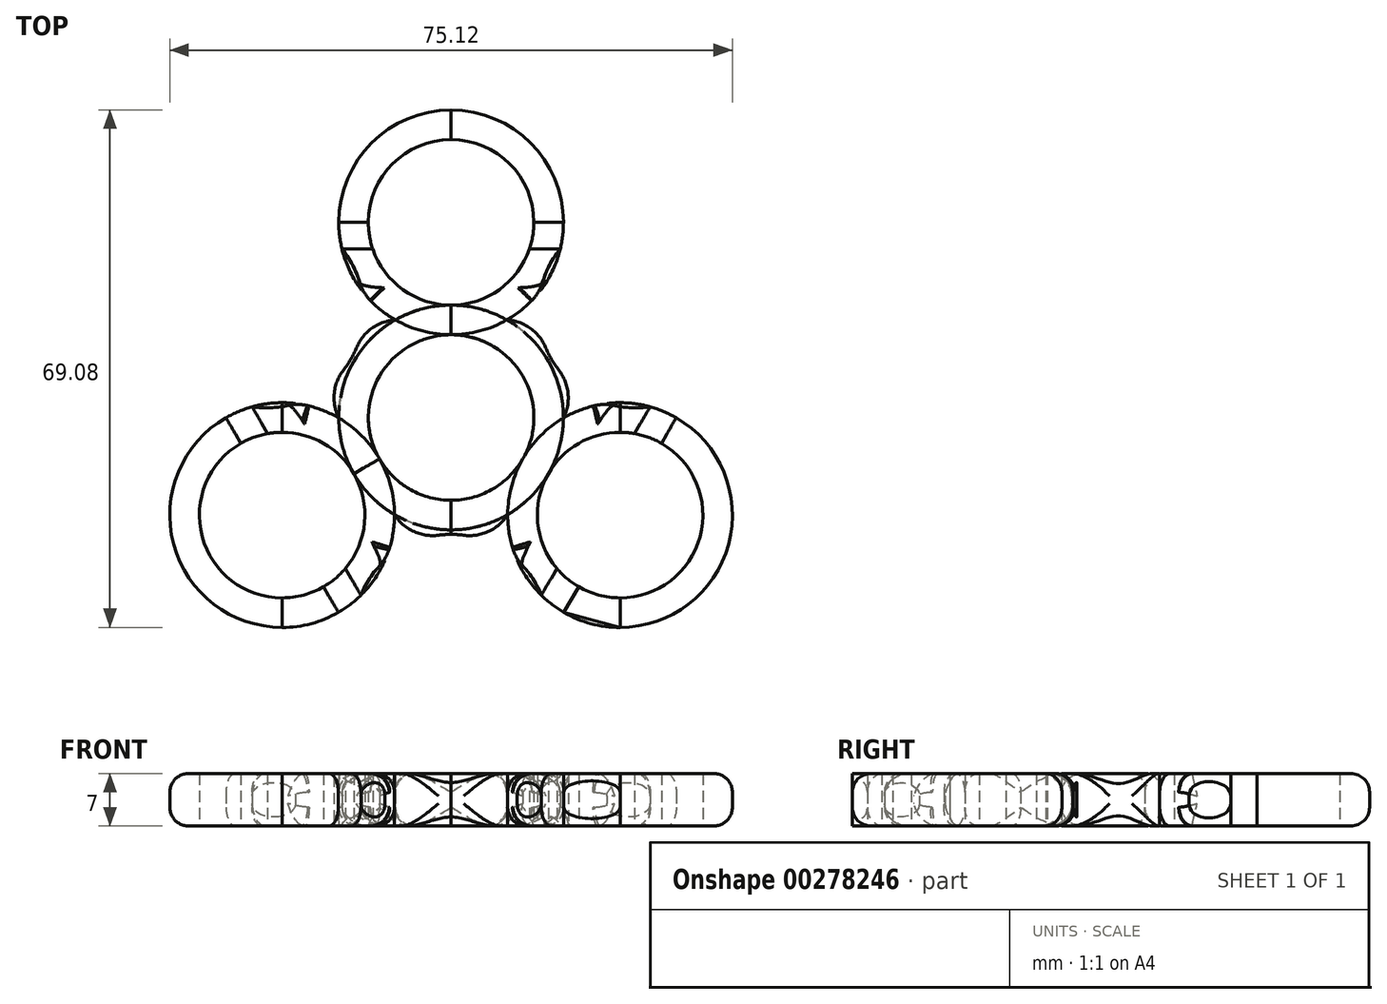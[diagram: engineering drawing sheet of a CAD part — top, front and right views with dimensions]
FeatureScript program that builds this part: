
annotation { "Feature Type Name" : "Feature", "Feature Type Description" : "" }
export const myFeature = defineFeature(function(context is Context, id is Id, definition is map)
    precondition{}
    {
        {
            var Q0;
            Q0=qCreatedBy(makeId("Top.planeOp"),FACE);
            var sketch = newSketch(context, id + "F0", { "sketchPlane" : qUnion([Q0])});
            skCircle(sketch, "E0", {"center": v(3.55, 32.56) * mm, "radius": 11.05 * mm});
            skCircle(sketch, "E1", {"center": v(3.55, 32.56) * mm, "radius": 15 * mm});
            skLineSegment(sketch, "E2", {"start": v(3.55, 32.56) * mm, "end": v(3.55, -19.54) * mm});
            skLineSegment(sketch, "E3", {"start": v(3.55, 17.56) * mm, "end": v(3.55, 6.5) * mm});
            skCircle(sketch, "E4", {"center": v(3.55, 6.5) * mm, "radius": 15 * mm});
            skCircle(sketch, "E5", {"center": v(3.55, 6.5) * mm, "radius": 11.05 * mm});
            skCircle(sketch, "E6.1.0", {"center": v(-19.01, -6.52) * mm, "radius": 11.05 * mm});
            skCircle(sketch, "E6.1.1", {"center": v(-19.01, -6.52) * mm, "radius": 15 * mm});
            skCircle(sketch, "E6.2.0", {"center": v(26.1, -6.52) * mm, "radius": 11.05 * mm});
            skCircle(sketch, "E6.2.1", {"center": v(26.1, -6.52) * mm, "radius": 15 * mm});
            skLineSegment(sketch, "E7", {"start": v(-19.01, -6.52) * mm, "end": v(-19.01, 16.07) * mm});
            skLineSegment(sketch, "E8", {"start": v(3.55, 32.56) * mm, "end": v(-11.45, 32.56) * mm});
            skLineSegment(sketch, "E9", {"start": v(-11.45, 32.56) * mm, "end": v(3.55, 32.56) * mm});
            skLineSegment(sketch, "E10", {"start": v(3.55, 32.56) * mm, "end": v(18.55, 32.56) * mm});
            skLineSegment(sketch, "E11", {"start": v(-19.01, -6.52) * mm, "end": v(-19.01, -21.52) * mm});
            skLineSegment(sketch, "E12", {"start": v(26.1, -6.52) * mm, "end": v(26.1, -21.52) * mm});
            skLineSegment(sketch, "E13", {"start": v(26.1, -21.52) * mm, "end": v(26.1, -6.52) * mm});
            skLineSegment(sketch, "E14", {"start": v(26.1, 8.48) * mm, "end": v(26.1, -6.52) * mm});
            skLineSegment(sketch, "E15", {"start": v(-19.01, -6.52) * mm, "end": v(-6.02, 0.98) * mm});
            skLineSegment(sketch, "E16", {"start": v(26.1, -6.52) * mm, "end": v(13.12, 0.98) * mm});
            skLineSegment(sketch, "E17", {"start": v(13.12, 0.98) * mm, "end": v(26.1, -6.52) * mm});
            skLineSegment(sketch, "E18", {"start": v(26.1, -6.52) * mm, "end": v(18.6, -19.5) * mm});
            skLineSegment(sketch, "E19", {"start": v(-19.01, -6.52) * mm, "end": v(-11.51, -19.5) * mm});
            skLineSegment(sketch, "E20", {"start": v(-11.51, -19.5) * mm, "end": v(-19.01, -6.52) * mm});
            skLineSegment(sketch, "E21", {"start": v(-19.01, -6.52) * mm, "end": v(-26.51, 6.47) * mm});
            skLineSegment(sketch, "E22", {"start": v(26.1, -6.52) * mm, "end": v(33.6, 6.47) * mm});
            skLineSegment(sketch, "E23", {"start": v(3.55, 32.56) * mm, "end": v(-5.63, 20.7) * mm, "construction": true});
            skLineSegment(sketch, "E24", {"start": v(-5.63, 20.7) * mm, "end": v(-1.04, 26.63) * mm, "construction": true});
            skLineSegment(sketch, "E25", {"start": v(26.1, -21.52) * mm, "end": v(18.6, -19.5) * mm});
            skLineSegment(sketch, "E26", {"start": v(26.1, -6.52) * mm, "end": v(19.61, -2.77) * mm});
            skLineSegment(sketch, "E27", {"start": v(16.54, -1) * mm, "end": v(22.86, -4.64) * mm});
            skLineSegment(sketch, "E28", {"start": v(22.86, -4.64) * mm, "end": v(15.6, -17.22) * mm});
            skLineSegment(sketch, "E29", {"start": v(-9.44, -1) * mm, "end": v(-15.76, -4.64) * mm});
            skLineSegment(sketch, "E30", {"start": v(-15.76, -4.64) * mm, "end": v(-8.5, -17.22) * mm});
            skLineSegment(sketch, "E31", {"start": v(-15.76, -4.64) * mm, "end": v(-23.03, 7.94) * mm});
            skLineSegment(sketch, "E32", {"start": v(22.86, -4.64) * mm, "end": v(30.12, 7.94) * mm});
            skLineSegment(sketch, "E33", {"start": v(3.55, 21.5) * mm, "end": v(3.55, 29) * mm});
            skLineSegment(sketch, "E34", {"start": v(3.55, 29) * mm, "end": v(-11.03, 29) * mm});
            skLineSegment(sketch, "E35", {"start": v(3.55, 29) * mm, "end": v(18.12, 29) * mm});
            skArc(sketch, "E36", {"start": v(15.6, -17.22) * mm, "mid": v(3.55, -9.1) * mm, "end": v(-8.5, -17.22) * mm});
            skArc(sketch, "E37", {"start": v(-23.03, 7.94) * mm, "mid": v(-9.8, 14.36) * mm, "end": v(-11.03, 29) * mm});
            skArc(sketch, "E38", {"start": v(18.12, 29) * mm, "mid": v(16.9, 14.36) * mm, "end": v(30.12, 7.94) * mm});
            skLineSegment(sketch, "E39", {"start": v(3.55, 6.5) * mm, "end": v(3.55, 47.56) * mm});
            skSolve(sketch);
        }
        {
            var Q0;
            {var subQ0=sQuery(id+"F0.wireOp",EDGE,"E4");var subQ1=sQuery(id+"F0.wireOp",EDGE,"E1");var subQ2=makeQuery(id+"F0.imprint","INTERSECT",VERTEX,{"disambiguationData":[OD(1.0)],"derivedFrom":[subQ1,subQ0]});Q0=makeQuery(id+"F0.imprint","IMPRINT",FACE,{"disambiguationData":[TD([[makeQuery(id+"F0.imprint","IMPRINT",EDGE,{"disambiguationData":[TD([[subQ2,1.0]])],"derivedFrom":subQ0}),1.0]])]});}
            var Q1;
            {var subQ0=sQuery(id+"F0.wireOp",EDGE,"E13");var subQ1=sQuery(id+"F0.wireOp",EDGE,"E6.2.0");var subQ2=makeQuery(id+"F0.imprint","INTERSECT",VERTEX,{"derivedFrom":[subQ1,subQ0]});Q1=makeQuery(id+"F0.imprint","IMPRINT",FACE,{"disambiguationData":[TD([[makeQuery(id+"F0.imprint","IMPRINT",EDGE,{"disambiguationData":[TD([[subQ2,-1.0]])],"derivedFrom":subQ1}),-1.0]])]});}
            var Q2;
            {var subQ1=sQuery(id+"F0.wireOp",EDGE,"E4");var subQ3=sQuery(id+"F0.wireOp",EDGE,"E6.1.1");var subQ4=makeQuery(id+"F0.imprint","INTERSECT",VERTEX,{"disambiguationData":[OD(0.0)],"derivedFrom":[subQ1,subQ3]});Q2=makeQuery(id+"F0.imprint","IMPRINT",FACE,{"disambiguationData":[TD([[makeQuery(id+"F0.imprint","IMPRINT",EDGE,{"disambiguationData":[TD([[subQ4,1.0]])],"derivedFrom":subQ3}),1.0]])]});}
            var Q3;
            {var subQ0=sQuery(id+"F0.wireOp",EDGE,"E5");var subQ1=sQuery(id+"F0.wireOp",EDGE,"E2");var subQ2=makeQuery(id+"F0.imprint","INTERSECT",VERTEX,{"derivedFrom":[subQ1,subQ0]});Q3=makeQuery(id+"F0.imprint","IMPRINT",FACE,{"disambiguationData":[TD([[makeQuery(id+"F0.imprint","IMPRINT",EDGE,{"disambiguationData":[TD([[subQ2,-1.0]])],"derivedFrom":subQ1}),1.0]])]});}
            var Q4;
            {var subQ0=sQuery(id+"F0.wireOp",EDGE,"E22");var subQ1=sQuery(id+"F0.wireOp",EDGE,"E6.2.0");var subQ2=makeQuery(id+"F0.imprint","INTERSECT",VERTEX,{"derivedFrom":[subQ1,subQ0]});Q4=makeQuery(id+"F0.imprint","IMPRINT",FACE,{"disambiguationData":[TD([[makeQuery(id+"F0.imprint","IMPRINT",EDGE,{"disambiguationData":[TD([[subQ2,-1.0]])],"derivedFrom":subQ1}),-1.0]])]});}
            var Q5;
            {var subQ0=sQuery(id+"F0.wireOp",EDGE,"E38");var subQ1=sQuery(id+"F0.wireOp",EDGE,"E6.2.1");var subQ2=makeQuery(id+"F0.imprint","INTERSECT",VERTEX,{"derivedFrom":[subQ1,subQ0]});Q5=makeQuery(id+"F0.imprint","IMPRINT",FACE,{"disambiguationData":[TD([[makeQuery(id+"F0.imprint","IMPRINT",EDGE,{"disambiguationData":[TD([[subQ2,-1.0]])],"derivedFrom":subQ1}),1.0]])]});}
            var Q6;
            {var subQ0=sQuery(id+"F0.wireOp",EDGE,"E17");Q6=makeQuery(id+"F0.imprint","IMPRINT",FACE,{"disambiguationData":[TD([[makeQuery(id+"F0.imprint","IMPRINT",EDGE,{"derivedFrom":subQ0}),-1.0]])]});}
            var Q7;
            {var subQ0=sQuery(id+"F0.wireOp",EDGE,"E18");var subQ1=sQuery(id+"F0.wireOp",EDGE,"E6.2.0");var subQ2=makeQuery(id+"F0.imprint","INTERSECT",VERTEX,{"derivedFrom":[subQ1,subQ0]});Q7=makeQuery(id+"F0.imprint","IMPRINT",FACE,{"disambiguationData":[TD([[makeQuery(id+"F0.imprint","IMPRINT",EDGE,{"disambiguationData":[TD([[subQ2,1.0]])],"derivedFrom":subQ1}),-1.0]])]});}
            var Q8;
            {var subQ0=sQuery(id+"F0.wireOp",EDGE,"E32");var subQ1=sQuery(id+"F0.wireOp",EDGE,"E6.2.0");var subQ2=makeQuery(id+"F0.imprint","INTERSECT",VERTEX,{"derivedFrom":[subQ1,subQ0]});Q8=makeQuery(id+"F0.imprint","IMPRINT",FACE,{"disambiguationData":[TD([[makeQuery(id+"F0.imprint","IMPRINT",EDGE,{"disambiguationData":[TD([[subQ2,-1.0]])],"derivedFrom":subQ1}),-1.0]])]});}
            var Q9;
            {var subQ0=sQuery(id+"F0.wireOp",EDGE,"E4");var subQ1=sQuery(id+"F0.wireOp",EDGE,"E1");var subQ2=makeQuery(id+"F0.imprint","INTERSECT",VERTEX,{"disambiguationData":[OD(0.0)],"derivedFrom":[subQ1,subQ0]});Q9=makeQuery(id+"F0.imprint","IMPRINT",FACE,{"disambiguationData":[TD([[makeQuery(id+"F0.imprint","IMPRINT",EDGE,{"disambiguationData":[TD([[subQ2,-1.0]])],"derivedFrom":subQ0}),1.0]])]});}
            var Q10;
            {var subQ0=sQuery(id+"F0.wireOp",EDGE,"E36");var subQ2=sQuery(id+"F0.wireOp",EDGE,"E6.1.1");var subQ6=makeQuery(id+"F0.imprint","INTERSECT",VERTEX,{"derivedFrom":[subQ2,subQ0]});Q10=makeQuery(id+"F0.imprint","IMPRINT",FACE,{"disambiguationData":[TD([[makeQuery(id+"F0.imprint","IMPRINT",EDGE,{"disambiguationData":[TD([[subQ6,-1.0]])],"derivedFrom":subQ2}),1.0]])]});}
            var Q11;
            {var subQ0=sQuery(id+"F0.wireOp",EDGE,"E36");var subQ1=sQuery(id+"F0.wireOp",EDGE,"E2");var subQ2=makeQuery(id+"F0.imprint","INTERSECT",VERTEX,{"derivedFrom":[subQ1,subQ0]});Q11=makeQuery(id+"F0.imprint","IMPRINT",FACE,{"disambiguationData":[TD([[makeQuery(id+"F0.imprint","IMPRINT",EDGE,{"disambiguationData":[TD([[subQ2,1.0]])],"derivedFrom":subQ1}),-1.0]])]});}
            var Q12;
            {var subQ0=sQuery(id+"F0.wireOp",EDGE,"E36");var subQ1=sQuery(id+"F0.wireOp",EDGE,"E2");var subQ2=makeQuery(id+"F0.imprint","INTERSECT",VERTEX,{"derivedFrom":[subQ1,subQ0]});Q12=makeQuery(id+"F0.imprint","IMPRINT",FACE,{"disambiguationData":[TD([[makeQuery(id+"F0.imprint","IMPRINT",EDGE,{"disambiguationData":[TD([[subQ2,1.0]])],"derivedFrom":subQ1}),1.0]])]});}
            var Q13;
            {var subQ1=sQuery(id+"F0.wireOp",EDGE,"E4");var subQ3=sQuery(id+"F0.wireOp",EDGE,"E6.1.1");var subQ4=makeQuery(id+"F0.imprint","INTERSECT",VERTEX,{"disambiguationData":[OD(1.0)],"derivedFrom":[subQ1,subQ3]});Q13=makeQuery(id+"F0.imprint","IMPRINT",FACE,{"disambiguationData":[TD([[makeQuery(id+"F0.imprint","IMPRINT",EDGE,{"disambiguationData":[TD([[subQ4,-1.0]])],"derivedFrom":subQ3}),1.0]])]});}
            var Q14;
            {var subQ0=sQuery(id+"F0.wireOp",EDGE,"E39");var subQ1=sQuery(id+"F0.wireOp",EDGE,"E0");var subQ2=makeQuery(id+"F0.imprint","INTERSECT",VERTEX,{"derivedFrom":[subQ1,subQ0]});Q14=makeQuery(id+"F0.imprint","IMPRINT",FACE,{"disambiguationData":[TD([[makeQuery(id+"F0.imprint","IMPRINT",EDGE,{"disambiguationData":[TD([[subQ2,-1.0]])],"derivedFrom":subQ1}),-1.0]])]});}
            var Q15;
            {var subQ0=sQuery(id+"F0.wireOp",EDGE,"E37");var subQ1=sQuery(id+"F0.wireOp",EDGE,"E1");var subQ2=makeQuery(id+"F0.imprint","INTERSECT",VERTEX,{"derivedFrom":[subQ1,subQ0]});Q15=makeQuery(id+"F0.imprint","IMPRINT",FACE,{"disambiguationData":[TD([[makeQuery(id+"F0.imprint","IMPRINT",EDGE,{"disambiguationData":[TD([[subQ2,-1.0]])],"derivedFrom":subQ1}),-1.0]])]});}
            var Q16;
            {var subQ0=sQuery(id+"F0.wireOp",EDGE,"E21");var subQ1=sQuery(id+"F0.wireOp",EDGE,"E6.1.0");var subQ2=makeQuery(id+"F0.imprint","INTERSECT",VERTEX,{"derivedFrom":[subQ1,subQ0]});Q16=makeQuery(id+"F0.imprint","IMPRINT",FACE,{"disambiguationData":[TD([[makeQuery(id+"F0.imprint","IMPRINT",EDGE,{"disambiguationData":[TD([[subQ2,1.0]])],"derivedFrom":subQ1}),-1.0]])]});}
            var Q17;
            {var subQ0=sQuery(id+"F0.wireOp",EDGE,"E9");var subQ1=sQuery(id+"F0.wireOp",EDGE,"E0");var subQ2=makeQuery(id+"F0.imprint","INTERSECT",VERTEX,{"derivedFrom":[subQ1,subQ0]});Q17=makeQuery(id+"F0.imprint","IMPRINT",FACE,{"disambiguationData":[TD([[makeQuery(id+"F0.imprint","IMPRINT",EDGE,{"disambiguationData":[TD([[subQ2,-1.0]])],"derivedFrom":subQ1}),-1.0]])]});}
            var Q18;
            {var subQ0=sQuery(id+"F0.wireOp",EDGE,"E17");Q18=makeQuery(id+"F0.imprint","IMPRINT",FACE,{"disambiguationData":[TD([[makeQuery(id+"F0.imprint","IMPRINT",EDGE,{"derivedFrom":subQ0}),1.0]])]});}
            var Q19;
            {var subQ0=sQuery(id+"F0.wireOp",EDGE,"E38");var subQ1=sQuery(id+"F0.wireOp",EDGE,"E1");var subQ2=makeQuery(id+"F0.imprint","INTERSECT",VERTEX,{"derivedFrom":[subQ1,subQ0]});Q19=makeQuery(id+"F0.imprint","IMPRINT",FACE,{"disambiguationData":[TD([[makeQuery(id+"F0.imprint","IMPRINT",EDGE,{"disambiguationData":[TD([[subQ2,1.0]])],"derivedFrom":subQ1}),-1.0]])]});}
            var Q20;
            {var subQ3=sQuery(id+"F0.wireOp",EDGE,"E37");var subQ5=sQuery(id+"F0.wireOp",EDGE,"E6.1.1");var subQ6=makeQuery(id+"F0.imprint","INTERSECT",VERTEX,{"derivedFrom":[subQ5,subQ3]});Q20=makeQuery(id+"F0.imprint","IMPRINT",FACE,{"disambiguationData":[TD([[makeQuery(id+"F0.imprint","IMPRINT",EDGE,{"disambiguationData":[TD([[subQ6,1.0]])],"derivedFrom":subQ5}),1.0]])]});}
            var Q21;
            {var subQ0=sQuery(id+"F0.wireOp",EDGE,"E36");var subQ2=sQuery(id+"F0.wireOp",EDGE,"E6.2.1");var subQ6=makeQuery(id+"F0.imprint","INTERSECT",VERTEX,{"derivedFrom":[subQ2,subQ0]});Q21=makeQuery(id+"F0.imprint","IMPRINT",FACE,{"disambiguationData":[TD([[makeQuery(id+"F0.imprint","IMPRINT",EDGE,{"disambiguationData":[TD([[subQ6,1.0]])],"derivedFrom":subQ2}),1.0]])]});}
            var Q22;
            {var subQ0=sQuery(id+"F0.wireOp",EDGE,"E38");var subQ1=sQuery(id+"F0.wireOp",EDGE,"E1");var subQ2=makeQuery(id+"F0.imprint","INTERSECT",VERTEX,{"derivedFrom":[subQ1,subQ0]});Q22=makeQuery(id+"F0.imprint","IMPRINT",FACE,{"disambiguationData":[TD([[makeQuery(id+"F0.imprint","IMPRINT",EDGE,{"disambiguationData":[TD([[subQ2,1.0]])],"derivedFrom":subQ1}),1.0]])]});}
            var Q23;
            {var subQ0=sQuery(id+"F0.wireOp",EDGE,"E10");var subQ1=sQuery(id+"F0.wireOp",EDGE,"E0");var subQ2=makeQuery(id+"F0.imprint","INTERSECT",VERTEX,{"derivedFrom":[subQ1,subQ0]});Q23=makeQuery(id+"F0.imprint","IMPRINT",FACE,{"disambiguationData":[TD([[makeQuery(id+"F0.imprint","IMPRINT",EDGE,{"disambiguationData":[TD([[subQ2,1.0]])],"derivedFrom":subQ1}),-1.0]])]});}
            var Q24;
            {var subQ0=sQuery(id+"F0.wireOp",EDGE,"E11");var subQ1=sQuery(id+"F0.wireOp",EDGE,"E6.1.0");var subQ2=makeQuery(id+"F0.imprint","INTERSECT",VERTEX,{"derivedFrom":[subQ1,subQ0]});Q24=makeQuery(id+"F0.imprint","IMPRINT",FACE,{"disambiguationData":[TD([[makeQuery(id+"F0.imprint","IMPRINT",EDGE,{"disambiguationData":[TD([[subQ2,-1.0]])],"derivedFrom":subQ1}),-1.0]])]});}
            var Q25;
            {var subQ0=sQuery(id+"F0.wireOp",EDGE,"E4");var subQ1=sQuery(id+"F0.wireOp",EDGE,"E1");var subQ2=makeQuery(id+"F0.imprint","INTERSECT",VERTEX,{"disambiguationData":[OD(1.0)],"derivedFrom":[subQ1,subQ0]});Q25=makeQuery(id+"F0.imprint","IMPRINT",FACE,{"disambiguationData":[TD([[makeQuery(id+"F0.imprint","IMPRINT",EDGE,{"disambiguationData":[TD([[subQ2,1.0]])],"derivedFrom":subQ1}),1.0]])]});}
            var Q26;
            {var subQ0=sQuery(id+"F0.wireOp",EDGE,"E7");var subQ1=sQuery(id+"F0.wireOp",EDGE,"E6.1.0");var subQ2=makeQuery(id+"F0.imprint","INTERSECT",VERTEX,{"derivedFrom":[subQ1,subQ0]});Q26=makeQuery(id+"F0.imprint","IMPRINT",FACE,{"disambiguationData":[TD([[makeQuery(id+"F0.imprint","IMPRINT",EDGE,{"disambiguationData":[TD([[subQ2,-1.0]])],"derivedFrom":subQ1}),-1.0]])]});}
            var Q27;
            {var subQ5=sQuery(id+"F0.wireOp",EDGE,"E25");Q27=makeQuery(id+"F0.imprint","IMPRINT",FACE,{"disambiguationData":[TD([[makeQuery(id+"F0.imprint","IMPRINT",EDGE,{"derivedFrom":subQ5}),-1.0]])]});}
            var Q28;
            {var subQ0=sQuery(id+"F0.wireOp",EDGE,"E5");var subQ1=sQuery(id+"F0.wireOp",EDGE,"E2");var subQ2=makeQuery(id+"F0.imprint","INTERSECT",VERTEX,{"derivedFrom":[subQ1,subQ0]});Q28=makeQuery(id+"F0.imprint","IMPRINT",FACE,{"disambiguationData":[TD([[makeQuery(id+"F0.imprint","IMPRINT",EDGE,{"disambiguationData":[TD([[subQ2,-1.0]])],"derivedFrom":subQ1}),-1.0]])]});}
            var Q29;
            {var subQ0=sQuery(id+"F0.wireOp",EDGE,"E20");var subQ1=sQuery(id+"F0.wireOp",EDGE,"E6.1.0");var subQ2=makeQuery(id+"F0.imprint","INTERSECT",VERTEX,{"derivedFrom":[subQ1,subQ0]});Q29=makeQuery(id+"F0.imprint","IMPRINT",FACE,{"disambiguationData":[TD([[makeQuery(id+"F0.imprint","IMPRINT",EDGE,{"disambiguationData":[TD([[subQ2,-1.0]])],"derivedFrom":subQ1}),-1.0]])]});}
            var Q30;
            {var subQ0=sQuery(id+"F0.wireOp",EDGE,"E39");var subQ1=sQuery(id+"F0.wireOp",EDGE,"E0");var subQ2=makeQuery(id+"F0.imprint","INTERSECT",VERTEX,{"derivedFrom":[subQ1,subQ0]});Q30=makeQuery(id+"F0.imprint","IMPRINT",FACE,{"disambiguationData":[TD([[makeQuery(id+"F0.imprint","IMPRINT",EDGE,{"disambiguationData":[TD([[subQ2,1.0]])],"derivedFrom":subQ1}),-1.0]])]});}
            var Q31;
            {var subQ0=sQuery(id+"F0.wireOp",EDGE,"E11");var subQ1=sQuery(id+"F0.wireOp",EDGE,"E6.1.0");var subQ2=makeQuery(id+"F0.imprint","INTERSECT",VERTEX,{"derivedFrom":[subQ1,subQ0]});Q31=makeQuery(id+"F0.imprint","IMPRINT",FACE,{"disambiguationData":[TD([[makeQuery(id+"F0.imprint","IMPRINT",EDGE,{"disambiguationData":[TD([[subQ2,1.0]])],"derivedFrom":subQ1}),-1.0]])]});}
            var Q32;
            {var subQ0=sQuery(id+"F0.wireOp",EDGE,"E37");var subQ2=sQuery(id+"F0.wireOp",EDGE,"E1");var subQ9=makeQuery(id+"F0.imprint","INTERSECT",VERTEX,{"derivedFrom":[subQ2,subQ0]});Q32=makeQuery(id+"F0.imprint","IMPRINT",FACE,{"disambiguationData":[TD([[makeQuery(id+"F0.imprint","IMPRINT",EDGE,{"disambiguationData":[TD([[subQ9,-1.0]])],"derivedFrom":subQ2}),1.0]])]});}
            var Q33;
            {var subQ0=sQuery(id+"F0.wireOp",EDGE,"E4");var subQ1=sQuery(id+"F0.wireOp",EDGE,"E1");var subQ2=makeQuery(id+"F0.imprint","INTERSECT",VERTEX,{"disambiguationData":[OD(0.0)],"derivedFrom":[subQ1,subQ0]});Q33=makeQuery(id+"F0.imprint","IMPRINT",FACE,{"disambiguationData":[TD([[makeQuery(id+"F0.imprint","IMPRINT",EDGE,{"disambiguationData":[TD([[subQ2,-1.0]])],"derivedFrom":subQ1}),1.0]])]});}
            var Q34;
            {var subQ1=sQuery(id+"F0.wireOp",EDGE,"E6.1.1");var subQ3=sQuery(id+"F0.wireOp",EDGE,"E7");var subQ4=makeQuery(id+"F0.imprint","INTERSECT",VERTEX,{"derivedFrom":[subQ1,subQ3]});Q34=makeQuery(id+"F0.imprint","IMPRINT",FACE,{"disambiguationData":[TD([[makeQuery(id+"F0.imprint","IMPRINT",EDGE,{"disambiguationData":[TD([[subQ4,1.0]])],"derivedFrom":subQ3}),1.0]])]});}
            var Q35;
            {var subQ0=sQuery(id+"F0.wireOp",EDGE,"E36");var subQ1=sQuery(id+"F0.wireOp",EDGE,"E6.2.1");var subQ3=makeQuery(id+"F0.imprint","INTERSECT",VERTEX,{"derivedFrom":[subQ1,subQ0]});Q35=makeQuery(id+"F0.imprint","IMPRINT",FACE,{"disambiguationData":[TD([[makeQuery(id+"F0.imprint","IMPRINT",EDGE,{"disambiguationData":[TD([[subQ3,-1.0]])],"derivedFrom":subQ1}),1.0]])]});}
            var Q36;
            {var subQ0=sQuery(id+"F0.wireOp",EDGE,"E37");var subQ1=sQuery(id+"F0.wireOp",EDGE,"E1");var subQ3=makeQuery(id+"F0.imprint","INTERSECT",VERTEX,{"derivedFrom":[subQ1,subQ0]});Q36=makeQuery(id+"F0.imprint","IMPRINT",FACE,{"disambiguationData":[TD([[makeQuery(id+"F0.imprint","IMPRINT",EDGE,{"disambiguationData":[TD([[subQ3,1.0]])],"derivedFrom":subQ1}),1.0]])]});}
            var Q37;
            {var subQ0=sQuery(id+"F0.wireOp",EDGE,"E36");var subQ1=sQuery(id+"F0.wireOp",EDGE,"E6.1.1");var subQ3=makeQuery(id+"F0.imprint","INTERSECT",VERTEX,{"derivedFrom":[subQ1,subQ0]});Q37=makeQuery(id+"F0.imprint","IMPRINT",FACE,{"disambiguationData":[TD([[makeQuery(id+"F0.imprint","IMPRINT",EDGE,{"disambiguationData":[TD([[subQ3,1.0]])],"derivedFrom":subQ1}),1.0]])]});}
            var Q38;
            {var subQ0=sQuery(id+"F0.wireOp",EDGE,"E14");var subQ1=sQuery(id+"F0.wireOp",EDGE,"E6.2.1");var subQ2=makeQuery(id+"F0.imprint","INTERSECT",VERTEX,{"derivedFrom":[subQ1,subQ0]});Q38=makeQuery(id+"F0.imprint","IMPRINT",FACE,{"disambiguationData":[TD([[makeQuery(id+"F0.imprint","IMPRINT",EDGE,{"disambiguationData":[TD([[subQ2,-1.0]])],"derivedFrom":subQ1}),1.0]])]});}
            var Q39;
            {var subQ0=sQuery(id+"F0.wireOp",EDGE,"E38");var subQ1=sQuery(id+"F0.wireOp",EDGE,"E1");var subQ3=makeQuery(id+"F0.imprint","INTERSECT",VERTEX,{"derivedFrom":[subQ1,subQ0]});Q39=makeQuery(id+"F0.imprint","IMPRINT",FACE,{"disambiguationData":[TD([[makeQuery(id+"F0.imprint","IMPRINT",EDGE,{"disambiguationData":[TD([[subQ3,-1.0]])],"derivedFrom":subQ1}),1.0]])]});}
            var Q40;
            {var subQ0=sQuery(id+"F0.wireOp",EDGE,"E25");Q40=makeQuery(id+"F0.imprint","IMPRINT",FACE,{"disambiguationData":[TD([[makeQuery(id+"F0.imprint","IMPRINT",EDGE,{"derivedFrom":subQ0}),1.0]])]});}
            var Q41;
            {var subQ0=sQuery(id+"F0.wireOp",EDGE,"E14");var subQ1=sQuery(id+"F0.wireOp",EDGE,"E6.2.1");var subQ2=makeQuery(id+"F0.imprint","INTERSECT",VERTEX,{"derivedFrom":[subQ1,subQ0]});Q41=makeQuery(id+"F0.imprint","IMPRINT",FACE,{"disambiguationData":[TD([[makeQuery(id+"F0.imprint","IMPRINT",EDGE,{"disambiguationData":[TD([[subQ2,-1.0]])],"derivedFrom":subQ0}),1.0]])]});}
            var Q42;
            {var subQ0=sQuery(id+"F0.wireOp",EDGE,"E7");var subQ1=sQuery(id+"F0.wireOp",EDGE,"E6.1.1");var subQ2=makeQuery(id+"F0.imprint","INTERSECT",VERTEX,{"derivedFrom":[subQ1,subQ0]});Q42=makeQuery(id+"F0.imprint","IMPRINT",FACE,{"disambiguationData":[TD([[makeQuery(id+"F0.imprint","IMPRINT",EDGE,{"disambiguationData":[TD([[subQ2,1.0]])],"derivedFrom":subQ1}),1.0]])]});}
            extrude(context, id + "F1", {"entities" : qUnion([Q0, Q1, Q2, Q3, Q4, Q5, Q6, Q7, Q8, Q9, Q10, Q11, Q12, Q13, Q14, Q15, Q16, Q17, Q18, Q19, Q20, Q21, Q22, Q23, Q24, Q25, Q26, Q27, Q28, Q29, Q30, Q31, Q32, Q33, Q34, Q35, Q36, Q37, Q38, Q39, Q40, Q41, Q42]), "depth" : 7 * mm, "offsetDistance" : 25 * mm});
        }
        {
            var Q0;
            Q0=makeQuery(id+"F1.opExtrude","SWEPT_EDGE",EDGE,{"disambiguationData":[OSD([sQuery(id+"F0.wireOp",EDGE,"E6.1.1"),sQuery(id+"F0.wireOp",EDGE,"E37")])]});
            var Q1;
            Q1=makeQuery(id+"F1.opExtrude","SWEPT_EDGE",EDGE,{"disambiguationData":[OSD([sQuery(id+"F0.wireOp",EDGE,"E1"),sQuery(id+"F0.wireOp",EDGE,"E37")])]});
            var Q2;
            Q2=makeQuery(id+"F1.opExtrude","SWEPT_EDGE",EDGE,{"disambiguationData":[OSD([sQuery(id+"F0.wireOp",EDGE,"E6.1.1"),sQuery(id+"F0.wireOp",EDGE,"E36")])]});
            var Q3;
            Q3=makeQuery(id+"F1.opExtrude","SWEPT_EDGE",EDGE,{"disambiguationData":[OSD([sQuery(id+"F0.wireOp",EDGE,"E6.2.1"),sQuery(id+"F0.wireOp",EDGE,"E36")])]});
            var Q4;
            Q4=makeQuery(id+"F1.opExtrude","SWEPT_EDGE",EDGE,{"disambiguationData":[OSD([sQuery(id+"F0.wireOp",EDGE,"E1"),sQuery(id+"F0.wireOp",EDGE,"E38")])]});
            var Q5;
            Q5=makeQuery(id+"F1.opExtrude","SWEPT_EDGE",EDGE,{"disambiguationData":[OSD([sQuery(id+"F0.wireOp",EDGE,"E6.2.1"),sQuery(id+"F0.wireOp",EDGE,"E38")])]});
            fillet(context, id + "F2", {"entities" : qUnion([Q0, Q1, Q2, Q3, Q4, Q5]), "radius" : 6 * mm, "tangentPropagation" : true, "allowEdgeOverflow" : false});
        }
        {
            var Q0;
            Q0=makeQuery(id+"F1.opExtrude","CAP_EDGE",EDGE,{"disambiguationData":[OSD([sQuery(id+"F0.wireOp",EDGE,"E37")])],"isStart":false});
            var Q1;
            {var subQ0=sQuery(id+"F0.wireOp",EDGE,"E37");var subQ1=sQuery(id+"F0.wireOp",EDGE,"E1");Q1=makeQuery(id+"F2.opFillet","BLEND_EDGE",EDGE,{"blendedFrom":[makeQuery(id+"F1.opExtrude","SWEPT_EDGE",EDGE,{"disambiguationData":[OSD([subQ1,subQ0])]}),makeQuery(id+"F1.opExtrude","CAP_FACE",FACE,{"disambiguationData":[OSD([sQuery(id+"F0.wireOp",EDGE,"E0"),subQ1,sQuery(id+"F0.wireOp",EDGE,"E5"),sQuery(id+"F0.wireOp",EDGE,"E6.1.0"),sQuery(id+"F0.wireOp",EDGE,"E6.1.1"),sQuery(id+"F0.wireOp",EDGE,"E6.2.0"),sQuery(id+"F0.wireOp",EDGE,"E6.2.1"),sQuery(id+"F0.wireOp",EDGE,"E36"),subQ0,sQuery(id+"F0.wireOp",EDGE,"E38")])],"isStart":false})],"blendedInto":[makeQuery(id+"F1.opExtrude","CAP_FACE",FACE,{"disambiguationData":[OSD([sQuery(id+"F0.wireOp",EDGE,"E0"),subQ1,sQuery(id+"F0.wireOp",EDGE,"E5"),sQuery(id+"F0.wireOp",EDGE,"E6.1.0"),sQuery(id+"F0.wireOp",EDGE,"E6.1.1"),sQuery(id+"F0.wireOp",EDGE,"E6.2.0"),sQuery(id+"F0.wireOp",EDGE,"E6.2.1"),sQuery(id+"F0.wireOp",EDGE,"E36"),subQ0,sQuery(id+"F0.wireOp",EDGE,"E38")])],"isStart":false})]});}
            var Q2;
            {var subQ0=sQuery(id+"F0.wireOp",EDGE,"E37");var subQ1=sQuery(id+"F0.wireOp",EDGE,"E6.1.1");Q2=makeQuery(id+"F2.opFillet","BLEND_EDGE",EDGE,{"blendedFrom":[makeQuery(id+"F1.opExtrude","SWEPT_EDGE",EDGE,{"disambiguationData":[OSD([subQ1,subQ0])]}),makeQuery(id+"F1.opExtrude","CAP_FACE",FACE,{"disambiguationData":[OSD([sQuery(id+"F0.wireOp",EDGE,"E0"),sQuery(id+"F0.wireOp",EDGE,"E1"),sQuery(id+"F0.wireOp",EDGE,"E5"),sQuery(id+"F0.wireOp",EDGE,"E6.1.0"),subQ1,sQuery(id+"F0.wireOp",EDGE,"E6.2.0"),sQuery(id+"F0.wireOp",EDGE,"E6.2.1"),sQuery(id+"F0.wireOp",EDGE,"E36"),subQ0,sQuery(id+"F0.wireOp",EDGE,"E38")])],"isStart":false})],"blendedInto":[makeQuery(id+"F1.opExtrude","CAP_FACE",FACE,{"disambiguationData":[OSD([sQuery(id+"F0.wireOp",EDGE,"E0"),sQuery(id+"F0.wireOp",EDGE,"E1"),sQuery(id+"F0.wireOp",EDGE,"E5"),sQuery(id+"F0.wireOp",EDGE,"E6.1.0"),subQ1,sQuery(id+"F0.wireOp",EDGE,"E6.2.0"),sQuery(id+"F0.wireOp",EDGE,"E6.2.1"),sQuery(id+"F0.wireOp",EDGE,"E36"),subQ0,sQuery(id+"F0.wireOp",EDGE,"E38")])],"isStart":false})]});}
            var Q3;
            {var subQ0=sQuery(id+"F0.wireOp",EDGE,"E37");var subQ1=sQuery(id+"F0.wireOp",EDGE,"E6.1.1");Q3=makeQuery(id+"F2.opFillet","BLEND_EDGE",EDGE,{"blendedFrom":[makeQuery(id+"F1.opExtrude","SWEPT_EDGE",EDGE,{"disambiguationData":[OSD([subQ1,subQ0])]}),makeQuery(id+"F1.opExtrude","CAP_FACE",FACE,{"disambiguationData":[OSD([sQuery(id+"F0.wireOp",EDGE,"E0"),sQuery(id+"F0.wireOp",EDGE,"E1"),sQuery(id+"F0.wireOp",EDGE,"E5"),sQuery(id+"F0.wireOp",EDGE,"E6.1.0"),subQ1,sQuery(id+"F0.wireOp",EDGE,"E6.2.0"),sQuery(id+"F0.wireOp",EDGE,"E6.2.1"),sQuery(id+"F0.wireOp",EDGE,"E36"),subQ0,sQuery(id+"F0.wireOp",EDGE,"E38")])],"isStart":true})],"blendedInto":[makeQuery(id+"F1.opExtrude","CAP_FACE",FACE,{"disambiguationData":[OSD([sQuery(id+"F0.wireOp",EDGE,"E0"),sQuery(id+"F0.wireOp",EDGE,"E1"),sQuery(id+"F0.wireOp",EDGE,"E5"),sQuery(id+"F0.wireOp",EDGE,"E6.1.0"),subQ1,sQuery(id+"F0.wireOp",EDGE,"E6.2.0"),sQuery(id+"F0.wireOp",EDGE,"E6.2.1"),sQuery(id+"F0.wireOp",EDGE,"E36"),subQ0,sQuery(id+"F0.wireOp",EDGE,"E38")])],"isStart":true})]});}
            var Q4;
            Q4=makeQuery(id+"F1.opExtrude","CAP_EDGE",EDGE,{"disambiguationData":[OSD([sQuery(id+"F0.wireOp",EDGE,"E37")])],"isStart":true});
            var Q5;
            {var subQ0=sQuery(id+"F0.wireOp",EDGE,"E37");var subQ1=sQuery(id+"F0.wireOp",EDGE,"E1");Q5=makeQuery(id+"F2.opFillet","BLEND_EDGE",EDGE,{"blendedFrom":[makeQuery(id+"F1.opExtrude","SWEPT_EDGE",EDGE,{"disambiguationData":[OSD([subQ1,subQ0])]}),makeQuery(id+"F1.opExtrude","CAP_FACE",FACE,{"disambiguationData":[OSD([sQuery(id+"F0.wireOp",EDGE,"E0"),subQ1,sQuery(id+"F0.wireOp",EDGE,"E5"),sQuery(id+"F0.wireOp",EDGE,"E6.1.0"),sQuery(id+"F0.wireOp",EDGE,"E6.1.1"),sQuery(id+"F0.wireOp",EDGE,"E6.2.0"),sQuery(id+"F0.wireOp",EDGE,"E6.2.1"),sQuery(id+"F0.wireOp",EDGE,"E36"),subQ0,sQuery(id+"F0.wireOp",EDGE,"E38")])],"isStart":true})],"blendedInto":[makeQuery(id+"F1.opExtrude","CAP_FACE",FACE,{"disambiguationData":[OSD([sQuery(id+"F0.wireOp",EDGE,"E0"),subQ1,sQuery(id+"F0.wireOp",EDGE,"E5"),sQuery(id+"F0.wireOp",EDGE,"E6.1.0"),sQuery(id+"F0.wireOp",EDGE,"E6.1.1"),sQuery(id+"F0.wireOp",EDGE,"E6.2.0"),sQuery(id+"F0.wireOp",EDGE,"E6.2.1"),sQuery(id+"F0.wireOp",EDGE,"E36"),subQ0,sQuery(id+"F0.wireOp",EDGE,"E38")])],"isStart":true})]});}
            var Q6;
            Q6=makeQuery(id+"F1.opExtrude","CAP_EDGE",EDGE,{"disambiguationData":[OSD([sQuery(id+"F0.wireOp",EDGE,"E38")])],"isStart":false});
            var Q7;
            Q7=makeQuery(id+"F1.opExtrude","CAP_EDGE",EDGE,{"disambiguationData":[OSD([sQuery(id+"F0.wireOp",EDGE,"E38")])],"isStart":true});
            var Q8;
            {var subQ0=sQuery(id+"F0.wireOp",EDGE,"E38");var subQ1=sQuery(id+"F0.wireOp",EDGE,"E6.2.1");Q8=makeQuery(id+"F2.opFillet","BLEND_EDGE",EDGE,{"blendedFrom":[makeQuery(id+"F1.opExtrude","SWEPT_EDGE",EDGE,{"disambiguationData":[OSD([subQ1,subQ0])]}),makeQuery(id+"F1.opExtrude","CAP_FACE",FACE,{"disambiguationData":[OSD([sQuery(id+"F0.wireOp",EDGE,"E0"),sQuery(id+"F0.wireOp",EDGE,"E1"),sQuery(id+"F0.wireOp",EDGE,"E5"),sQuery(id+"F0.wireOp",EDGE,"E6.1.0"),sQuery(id+"F0.wireOp",EDGE,"E6.1.1"),sQuery(id+"F0.wireOp",EDGE,"E6.2.0"),subQ1,sQuery(id+"F0.wireOp",EDGE,"E36"),sQuery(id+"F0.wireOp",EDGE,"E37"),subQ0])],"isStart":true})],"blendedInto":[makeQuery(id+"F1.opExtrude","CAP_FACE",FACE,{"disambiguationData":[OSD([sQuery(id+"F0.wireOp",EDGE,"E0"),sQuery(id+"F0.wireOp",EDGE,"E1"),sQuery(id+"F0.wireOp",EDGE,"E5"),sQuery(id+"F0.wireOp",EDGE,"E6.1.0"),sQuery(id+"F0.wireOp",EDGE,"E6.1.1"),sQuery(id+"F0.wireOp",EDGE,"E6.2.0"),subQ1,sQuery(id+"F0.wireOp",EDGE,"E36"),sQuery(id+"F0.wireOp",EDGE,"E37"),subQ0])],"isStart":true})]});}
            var Q9;
            {var subQ0=sQuery(id+"F0.wireOp",EDGE,"E38");var subQ1=sQuery(id+"F0.wireOp",EDGE,"E6.2.1");Q9=makeQuery(id+"F2.opFillet","BLEND_EDGE",EDGE,{"blendedFrom":[makeQuery(id+"F1.opExtrude","SWEPT_EDGE",EDGE,{"disambiguationData":[OSD([subQ1,subQ0])]}),makeQuery(id+"F1.opExtrude","CAP_FACE",FACE,{"disambiguationData":[OSD([sQuery(id+"F0.wireOp",EDGE,"E0"),sQuery(id+"F0.wireOp",EDGE,"E1"),sQuery(id+"F0.wireOp",EDGE,"E5"),sQuery(id+"F0.wireOp",EDGE,"E6.1.0"),sQuery(id+"F0.wireOp",EDGE,"E6.1.1"),sQuery(id+"F0.wireOp",EDGE,"E6.2.0"),subQ1,sQuery(id+"F0.wireOp",EDGE,"E36"),sQuery(id+"F0.wireOp",EDGE,"E37"),subQ0])],"isStart":false})],"blendedInto":[makeQuery(id+"F1.opExtrude","CAP_FACE",FACE,{"disambiguationData":[OSD([sQuery(id+"F0.wireOp",EDGE,"E0"),sQuery(id+"F0.wireOp",EDGE,"E1"),sQuery(id+"F0.wireOp",EDGE,"E5"),sQuery(id+"F0.wireOp",EDGE,"E6.1.0"),sQuery(id+"F0.wireOp",EDGE,"E6.1.1"),sQuery(id+"F0.wireOp",EDGE,"E6.2.0"),subQ1,sQuery(id+"F0.wireOp",EDGE,"E36"),sQuery(id+"F0.wireOp",EDGE,"E37"),subQ0])],"isStart":false})]});}
            var Q10;
            {var subQ0=sQuery(id+"F0.wireOp",EDGE,"E38");var subQ1=sQuery(id+"F0.wireOp",EDGE,"E1");Q10=makeQuery(id+"F2.opFillet","BLEND_EDGE",EDGE,{"blendedFrom":[makeQuery(id+"F1.opExtrude","SWEPT_EDGE",EDGE,{"disambiguationData":[OSD([subQ1,subQ0])]}),makeQuery(id+"F1.opExtrude","CAP_FACE",FACE,{"disambiguationData":[OSD([sQuery(id+"F0.wireOp",EDGE,"E0"),subQ1,sQuery(id+"F0.wireOp",EDGE,"E5"),sQuery(id+"F0.wireOp",EDGE,"E6.1.0"),sQuery(id+"F0.wireOp",EDGE,"E6.1.1"),sQuery(id+"F0.wireOp",EDGE,"E6.2.0"),sQuery(id+"F0.wireOp",EDGE,"E6.2.1"),sQuery(id+"F0.wireOp",EDGE,"E36"),sQuery(id+"F0.wireOp",EDGE,"E37"),subQ0])],"isStart":true})],"blendedInto":[makeQuery(id+"F1.opExtrude","CAP_FACE",FACE,{"disambiguationData":[OSD([sQuery(id+"F0.wireOp",EDGE,"E0"),subQ1,sQuery(id+"F0.wireOp",EDGE,"E5"),sQuery(id+"F0.wireOp",EDGE,"E6.1.0"),sQuery(id+"F0.wireOp",EDGE,"E6.1.1"),sQuery(id+"F0.wireOp",EDGE,"E6.2.0"),sQuery(id+"F0.wireOp",EDGE,"E6.2.1"),sQuery(id+"F0.wireOp",EDGE,"E36"),sQuery(id+"F0.wireOp",EDGE,"E37"),subQ0])],"isStart":true})]});}
            var Q11;
            {var subQ0=sQuery(id+"F0.wireOp",EDGE,"E38");var subQ1=sQuery(id+"F0.wireOp",EDGE,"E1");Q11=makeQuery(id+"F2.opFillet","BLEND_EDGE",EDGE,{"blendedFrom":[makeQuery(id+"F1.opExtrude","SWEPT_EDGE",EDGE,{"disambiguationData":[OSD([subQ1,subQ0])]}),makeQuery(id+"F1.opExtrude","CAP_FACE",FACE,{"disambiguationData":[OSD([sQuery(id+"F0.wireOp",EDGE,"E0"),subQ1,sQuery(id+"F0.wireOp",EDGE,"E5"),sQuery(id+"F0.wireOp",EDGE,"E6.1.0"),sQuery(id+"F0.wireOp",EDGE,"E6.1.1"),sQuery(id+"F0.wireOp",EDGE,"E6.2.0"),sQuery(id+"F0.wireOp",EDGE,"E6.2.1"),sQuery(id+"F0.wireOp",EDGE,"E36"),sQuery(id+"F0.wireOp",EDGE,"E37"),subQ0])],"isStart":false})],"blendedInto":[makeQuery(id+"F1.opExtrude","CAP_FACE",FACE,{"disambiguationData":[OSD([sQuery(id+"F0.wireOp",EDGE,"E0"),subQ1,sQuery(id+"F0.wireOp",EDGE,"E5"),sQuery(id+"F0.wireOp",EDGE,"E6.1.0"),sQuery(id+"F0.wireOp",EDGE,"E6.1.1"),sQuery(id+"F0.wireOp",EDGE,"E6.2.0"),sQuery(id+"F0.wireOp",EDGE,"E6.2.1"),sQuery(id+"F0.wireOp",EDGE,"E36"),sQuery(id+"F0.wireOp",EDGE,"E37"),subQ0])],"isStart":false})]});}
            var Q12;
            {var subQ0=sQuery(id+"F0.wireOp",EDGE,"E36");var subQ1=sQuery(id+"F0.wireOp",EDGE,"E6.2.1");Q12=makeQuery(id+"F2.opFillet","BLEND_EDGE",EDGE,{"blendedFrom":[makeQuery(id+"F1.opExtrude","SWEPT_EDGE",EDGE,{"disambiguationData":[OSD([subQ1,subQ0])]}),makeQuery(id+"F1.opExtrude","CAP_FACE",FACE,{"disambiguationData":[OSD([sQuery(id+"F0.wireOp",EDGE,"E0"),sQuery(id+"F0.wireOp",EDGE,"E1"),sQuery(id+"F0.wireOp",EDGE,"E5"),sQuery(id+"F0.wireOp",EDGE,"E6.1.0"),sQuery(id+"F0.wireOp",EDGE,"E6.1.1"),sQuery(id+"F0.wireOp",EDGE,"E6.2.0"),subQ1,subQ0,sQuery(id+"F0.wireOp",EDGE,"E37"),sQuery(id+"F0.wireOp",EDGE,"E38")])],"isStart":false})],"blendedInto":[makeQuery(id+"F1.opExtrude","CAP_FACE",FACE,{"disambiguationData":[OSD([sQuery(id+"F0.wireOp",EDGE,"E0"),sQuery(id+"F0.wireOp",EDGE,"E1"),sQuery(id+"F0.wireOp",EDGE,"E5"),sQuery(id+"F0.wireOp",EDGE,"E6.1.0"),sQuery(id+"F0.wireOp",EDGE,"E6.1.1"),sQuery(id+"F0.wireOp",EDGE,"E6.2.0"),subQ1,subQ0,sQuery(id+"F0.wireOp",EDGE,"E37"),sQuery(id+"F0.wireOp",EDGE,"E38")])],"isStart":false})]});}
            var Q13;
            Q13=makeQuery(id+"F1.opExtrude","CAP_EDGE",EDGE,{"disambiguationData":[OSD([sQuery(id+"F0.wireOp",EDGE,"E36")])],"isStart":false});
            var Q14;
            {var subQ0=sQuery(id+"F0.wireOp",EDGE,"E36");var subQ1=sQuery(id+"F0.wireOp",EDGE,"E6.2.1");Q14=makeQuery(id+"F2.opFillet","BLEND_EDGE",EDGE,{"blendedFrom":[makeQuery(id+"F1.opExtrude","SWEPT_EDGE",EDGE,{"disambiguationData":[OSD([subQ1,subQ0])]}),makeQuery(id+"F1.opExtrude","CAP_FACE",FACE,{"disambiguationData":[OSD([sQuery(id+"F0.wireOp",EDGE,"E0"),sQuery(id+"F0.wireOp",EDGE,"E1"),sQuery(id+"F0.wireOp",EDGE,"E5"),sQuery(id+"F0.wireOp",EDGE,"E6.1.0"),sQuery(id+"F0.wireOp",EDGE,"E6.1.1"),sQuery(id+"F0.wireOp",EDGE,"E6.2.0"),subQ1,subQ0,sQuery(id+"F0.wireOp",EDGE,"E37"),sQuery(id+"F0.wireOp",EDGE,"E38")])],"isStart":true})],"blendedInto":[makeQuery(id+"F1.opExtrude","CAP_FACE",FACE,{"disambiguationData":[OSD([sQuery(id+"F0.wireOp",EDGE,"E0"),sQuery(id+"F0.wireOp",EDGE,"E1"),sQuery(id+"F0.wireOp",EDGE,"E5"),sQuery(id+"F0.wireOp",EDGE,"E6.1.0"),sQuery(id+"F0.wireOp",EDGE,"E6.1.1"),sQuery(id+"F0.wireOp",EDGE,"E6.2.0"),subQ1,subQ0,sQuery(id+"F0.wireOp",EDGE,"E37"),sQuery(id+"F0.wireOp",EDGE,"E38")])],"isStart":true})]});}
            var Q15;
            Q15=makeQuery(id+"F1.opExtrude","CAP_EDGE",EDGE,{"disambiguationData":[OSD([sQuery(id+"F0.wireOp",EDGE,"E36")])],"isStart":true});
            var Q16;
            {var subQ0=sQuery(id+"F0.wireOp",EDGE,"E36");var subQ1=sQuery(id+"F0.wireOp",EDGE,"E6.1.1");Q16=makeQuery(id+"F2.opFillet","BLEND_EDGE",EDGE,{"blendedFrom":[makeQuery(id+"F1.opExtrude","SWEPT_EDGE",EDGE,{"disambiguationData":[OSD([subQ1,subQ0])]}),makeQuery(id+"F1.opExtrude","CAP_FACE",FACE,{"disambiguationData":[OSD([sQuery(id+"F0.wireOp",EDGE,"E0"),sQuery(id+"F0.wireOp",EDGE,"E1"),sQuery(id+"F0.wireOp",EDGE,"E5"),sQuery(id+"F0.wireOp",EDGE,"E6.1.0"),subQ1,sQuery(id+"F0.wireOp",EDGE,"E6.2.0"),sQuery(id+"F0.wireOp",EDGE,"E6.2.1"),subQ0,sQuery(id+"F0.wireOp",EDGE,"E37"),sQuery(id+"F0.wireOp",EDGE,"E38")])],"isStart":true})],"blendedInto":[makeQuery(id+"F1.opExtrude","CAP_FACE",FACE,{"disambiguationData":[OSD([sQuery(id+"F0.wireOp",EDGE,"E0"),sQuery(id+"F0.wireOp",EDGE,"E1"),sQuery(id+"F0.wireOp",EDGE,"E5"),sQuery(id+"F0.wireOp",EDGE,"E6.1.0"),subQ1,sQuery(id+"F0.wireOp",EDGE,"E6.2.0"),sQuery(id+"F0.wireOp",EDGE,"E6.2.1"),subQ0,sQuery(id+"F0.wireOp",EDGE,"E37"),sQuery(id+"F0.wireOp",EDGE,"E38")])],"isStart":true})]});}
            var Q17;
            {var subQ0=sQuery(id+"F0.wireOp",EDGE,"E36");var subQ1=sQuery(id+"F0.wireOp",EDGE,"E6.1.1");Q17=makeQuery(id+"F2.opFillet","BLEND_EDGE",EDGE,{"blendedFrom":[makeQuery(id+"F1.opExtrude","SWEPT_EDGE",EDGE,{"disambiguationData":[OSD([subQ1,subQ0])]}),makeQuery(id+"F1.opExtrude","CAP_FACE",FACE,{"disambiguationData":[OSD([sQuery(id+"F0.wireOp",EDGE,"E0"),sQuery(id+"F0.wireOp",EDGE,"E1"),sQuery(id+"F0.wireOp",EDGE,"E5"),sQuery(id+"F0.wireOp",EDGE,"E6.1.0"),subQ1,sQuery(id+"F0.wireOp",EDGE,"E6.2.0"),sQuery(id+"F0.wireOp",EDGE,"E6.2.1"),subQ0,sQuery(id+"F0.wireOp",EDGE,"E37"),sQuery(id+"F0.wireOp",EDGE,"E38")])],"isStart":false})],"blendedInto":[makeQuery(id+"F1.opExtrude","CAP_FACE",FACE,{"disambiguationData":[OSD([sQuery(id+"F0.wireOp",EDGE,"E0"),sQuery(id+"F0.wireOp",EDGE,"E1"),sQuery(id+"F0.wireOp",EDGE,"E5"),sQuery(id+"F0.wireOp",EDGE,"E6.1.0"),subQ1,sQuery(id+"F0.wireOp",EDGE,"E6.2.0"),sQuery(id+"F0.wireOp",EDGE,"E6.2.1"),subQ0,sQuery(id+"F0.wireOp",EDGE,"E37"),sQuery(id+"F0.wireOp",EDGE,"E38")])],"isStart":false})]});}
            fillet(context, id + "F3", {"entities" : qUnion([Q0, Q1, Q2, Q3, Q4, Q5, Q6, Q7, Q8, Q9, Q10, Q11, Q12, Q13, Q14, Q15, Q16, Q17]), "radius" : 3 * mm, "allowEdgeOverflow" : false});
        }
        {
            var Q0;
            Q0=makeQuery(id+"F1.opExtrude","CAP_EDGE",EDGE,{"disambiguationData":[OSD([sQuery(id+"F0.wireOp",EDGE,"E6.1.1")])],"isStart":true});
            var Q1;
            Q1=makeQuery(id+"F1.opExtrude","CAP_EDGE",EDGE,{"disambiguationData":[OSD([sQuery(id+"F0.wireOp",EDGE,"E6.1.1")])],"isStart":false});
            var Q2;
            Q2=makeQuery(id+"F1.opExtrude","CAP_EDGE",EDGE,{"disambiguationData":[OSD([sQuery(id+"F0.wireOp",EDGE,"E1")])],"isStart":true});
            var Q3;
            Q3=makeQuery(id+"F1.opExtrude","CAP_EDGE",EDGE,{"disambiguationData":[OSD([sQuery(id+"F0.wireOp",EDGE,"E1")])],"isStart":false});
            var Q4;
            Q4=makeQuery(id+"F1.opExtrude","CAP_EDGE",EDGE,{"disambiguationData":[OSD([sQuery(id+"F0.wireOp",EDGE,"E6.2.1")])],"isStart":true});
            var Q5;
            Q5=makeQuery(id+"F1.opExtrude","CAP_EDGE",EDGE,{"disambiguationData":[OSD([sQuery(id+"F0.wireOp",EDGE,"E6.2.1")])],"isStart":false});
            fillet(context, id + "F4", {"entities" : qUnion([Q0, Q1, Q2, Q3, Q4, Q5]), "radius" : 2.5 * mm, "tangentPropagation" : true, "allowEdgeOverflow" : false});
        }
    });
